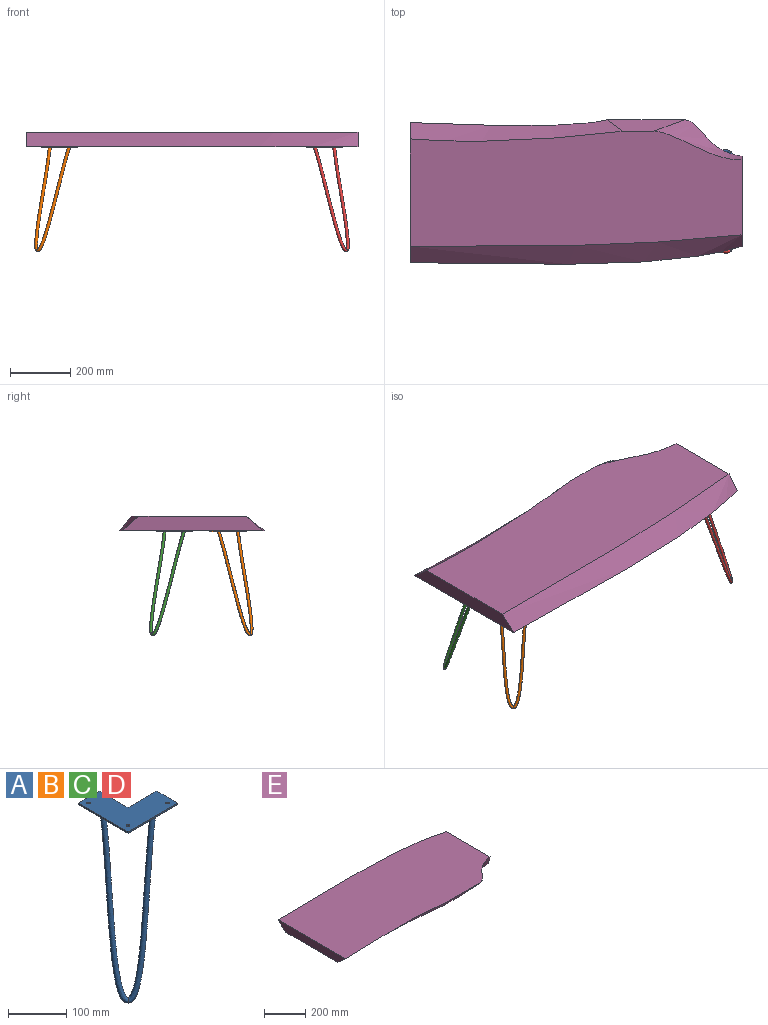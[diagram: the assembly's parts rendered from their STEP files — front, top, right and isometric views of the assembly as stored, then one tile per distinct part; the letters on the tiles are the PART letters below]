
ASSEMBLY  parts=5 mates=4
PART A: 13 faces, bbox 142.4x142.4x347.6 mm
  f0: plane 120.65x120.65mm, normal (0,0,1), area 9582.4mm2, adj f1,f2,f3,f4,f5,f6,f7,f8
  f1: plane 120.65x3.18mm, normal (0,-1,0), area 383.1mm2, adj f0,f2,f9,f10
  f2: plane 120.65x3.18mm, normal (-1,0,0), area 383.1mm2, adj f0,f1,f3,f10
  f3: plane 50.8x3.18mm, normal (0,1,0), area 161.3mm2, adj f0,f2,f4,f10
  f4: plane 69.85x3.18mm, normal (1,0,0), area 221.8mm2, adj f0,f3,f5,f10
  f5: plane 69.85x3.18mm, normal (0,1,0), area 221.8mm2, adj f0,f4,f9,f10
  f6: cylinder r=3.17mm len=6.35mm, axis (0,0,1), area 63.3mm2, adj f0,f10
  f7: cylinder r=3.17mm len=6.35mm, axis (0,0,1), area 63.3mm2, adj f0,f10
  f8: cylinder r=3.17mm len=6.35mm, axis (0,0,1), area 63.3mm2, adj f0,f10
  f9: plane 50.8x3.18mm, normal (1,0,0), area 161.3mm2, adj f0,f1,f5,f10
  f10: plane 120.65x120.65mm, normal (0,0,-1), area 9431.4mm2, adj f1,f2,f3,f4,f5,f6,f7,f8
  f11: bspline ~347.48x111.46mm, area 10818.1mm2, adj f10,f12
  f12: bspline ~347.48x111.46mm, area 10818.1mm2, adj f10,f11
PART B: same geometry as A
PART C: same geometry as A
PART D: same geometry as A
PART E: 8 faces, bbox 1110x513.8x59 mm
  f0: plane 1098.55x496.64mm, normal (0,0,1), area 492510.9mm2, adj f2,f3,f4,f5,f6,f7
  f1: plane 1109.97x392.42mm, normal (0,0,-1), area 375907.4mm2, adj f2,f3,f4,f5,f6,f7
  f2: bspline ~1098.55x121.4mm, area 82573.6mm2, adj f0,f1,f3,f7
  f3: plane 298.45x47.63mm, normal (1,0,0), area 13004mm2, adj f0,f1,f2,f4
  f4: bspline ~444.5x133.35mm, area 17467.7mm2, adj f0,f1,f3,f5
  f5: plane 254x47.63mm, normal (0,-0.78,-0.62), area 10844mm2, adj f0,f1,f4,f6
  f6: bspline ~704.85x82.64mm, area 46493.4mm2, adj f0,f1,f5,f7
  f7: plane 463.55x47.63mm, normal (-1,0,0), area 19506mm2, adj f0,f1,f2,f6
PLACE A rot(axis=(0,0,1),180deg) t=(66.58,-29.1,63.5)mm
PLACE B t=(-35.02,-22.75,63.5)mm
PLACE C rot(axis=(0,0,-1),90deg) t=(-330.29,-324.37,63.5)mm
PLACE D rot(axis=(0,0,1),90deg) t=(361.86,272.53,63.5)mm
PLACE E rot(axis=(1,0,0),180deg) t=(15.78,2.65,796.92)mm
MATE fastened D.f0 <-> E.f0  axis (0,0,-1) through (463.46,-124.35,406.4)mm
MATE fastened C.f0 <-> E.f0  axis (0,0,-1) through (-431.89,72.5,406.4)mm
MATE fastened A.f0 <-> E.f0  axis (0,0,-1) through (463.46,72.5,406.4)mm
MATE fastened B.f0 <-> E.f0  axis (0,0,-1) through (-431.89,-124.35,406.4)mm
